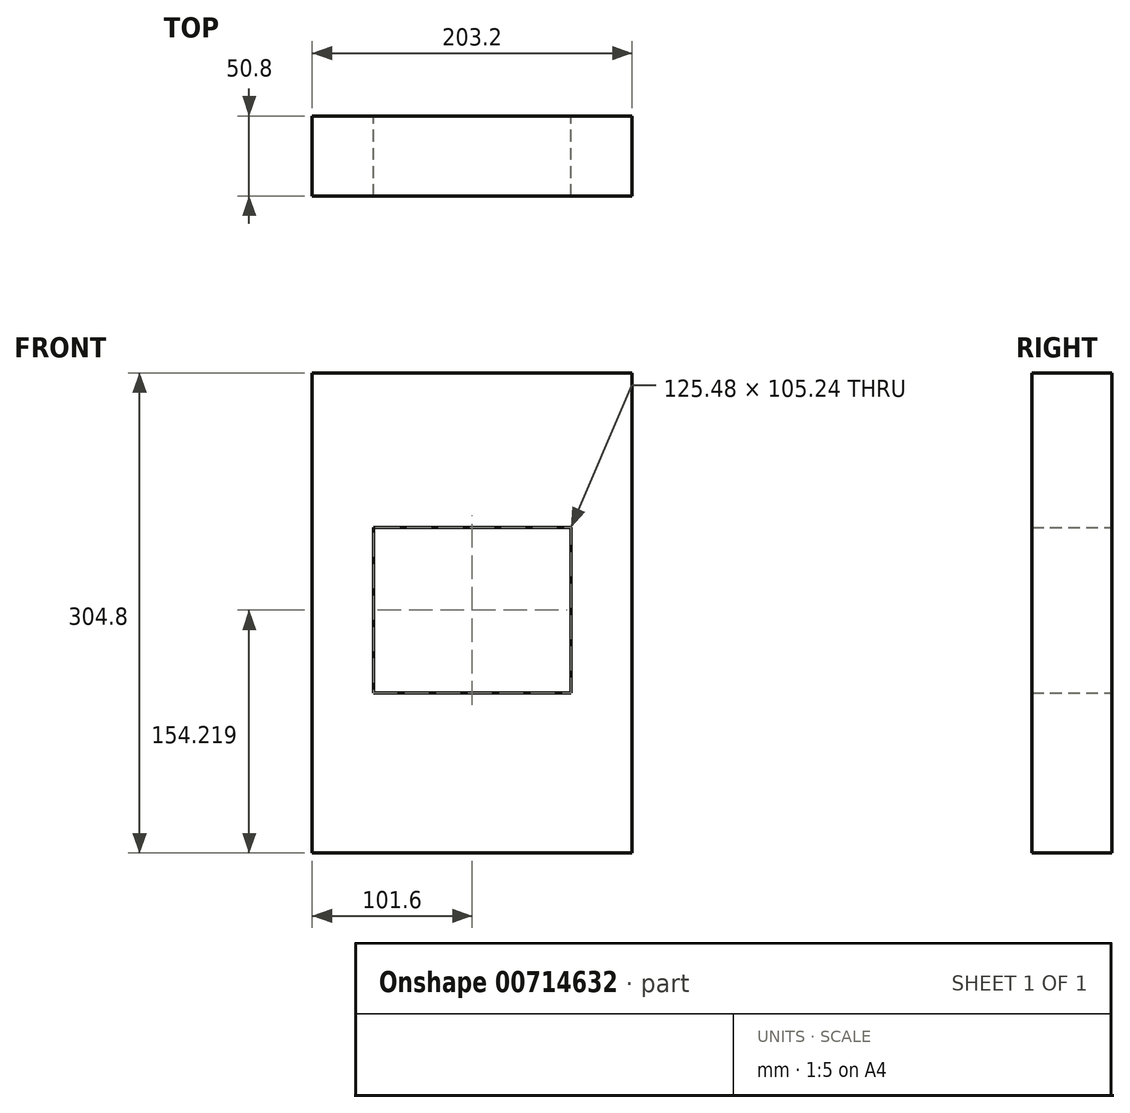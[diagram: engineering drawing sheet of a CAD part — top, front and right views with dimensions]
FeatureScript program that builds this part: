
annotation { "Feature Type Name" : "Feature", "Feature Type Description" : "" }
export const myFeature = defineFeature(function(context is Context, id is Id, definition is map)
    precondition{}
    {
        {
            var Q0;
            Q0=qCreatedBy(makeId("Front.planeOp"),FACE);
            var sketch = newSketch(context, id + "F0", { "sketchPlane" : qUnion([Q0])});
            skLineSegment(sketch, "E0.bottom", {"start": v(-101.6, 152.4) * mm, "end": v(101.6, 152.4) * mm});
            skLineSegment(sketch, "E0.top", {"start": v(-101.6, -152.4) * mm, "end": v(101.6, -152.4) * mm});
            skLineSegment(sketch, "E0.left", {"start": v(-101.6, 152.4) * mm, "end": v(-101.6, -152.4) * mm});
            skLineSegment(sketch, "E0.right", {"start": v(101.6, 152.4) * mm, "end": v(101.6, -152.4) * mm});
            skLineSegment(sketch, "E1.bottom", {"start": v(-38.86, -50.8) * mm, "end": v(38.86, -50.8) * mm});
            skLineSegment(sketch, "E1.top", {"start": v(-38.86, -109.74) * mm, "end": v(38.86, -109.74) * mm});
            skLineSegment(sketch, "E1.left", {"start": v(-38.86, -50.8) * mm, "end": v(-38.86, -109.74) * mm});
            skLineSegment(sketch, "E1.right", {"start": v(38.86, -50.8) * mm, "end": v(38.86, -109.74) * mm});
            skLineSegment(sketch, "E2.bottom", {"start": v(-62.74, 114.3) * mm, "end": v(62.74, 114.3) * mm});
            skLineSegment(sketch, "E2.top", {"start": v(-62.74, 54.44) * mm, "end": v(62.74, 54.44) * mm});
            skLineSegment(sketch, "E2.left", {"start": v(-62.74, 114.3) * mm, "end": v(-62.74, 54.44) * mm});
            skLineSegment(sketch, "E2.right", {"start": v(62.74, 114.3) * mm, "end": v(62.74, 54.44) * mm});
            skLineSegment(sketch, "E3", {"start": v(62.74, 54.44) * mm, "end": v(62.74, -50.8) * mm});
            skLineSegment(sketch, "E4", {"start": v(62.74, -50.8) * mm, "end": v(-62.74, -50.8) * mm});
            skLineSegment(sketch, "E5", {"start": v(-62.74, 54.44) * mm, "end": v(-62.74, -50.8) * mm});
            skSolve(sketch);
        }
        {
            var Q0;
            Q0=qSketchRegion(id+"F0",true);
            var Q1;
            Q1=makeQuery(id+"F0.imprint","IMPRINT",FACE,{"disambiguationData":[TD([[makeQuery(id+"F0.imprint","IMPRINT",EDGE,{"derivedFrom":sQuery(id+"F0.wireOp",EDGE,"E2.bottom")}),-1.0]])]});
            var Q2;
            Q2=makeQuery(id+"F0.imprint","IMPRINT",FACE,{"disambiguationData":[TD([[makeQuery(id+"F0.imprint","IMPRINT",EDGE,{"derivedFrom":sQuery(id+"F0.wireOp",EDGE,"E1.top")}),1.0]])]});
            extrude(context, id + "F1", {"entities" : qUnion([Q0, Q1, Q2]), "depth" : 50.8 * mm, "offsetDistance" : 25.4 * mm});
        }
    });
